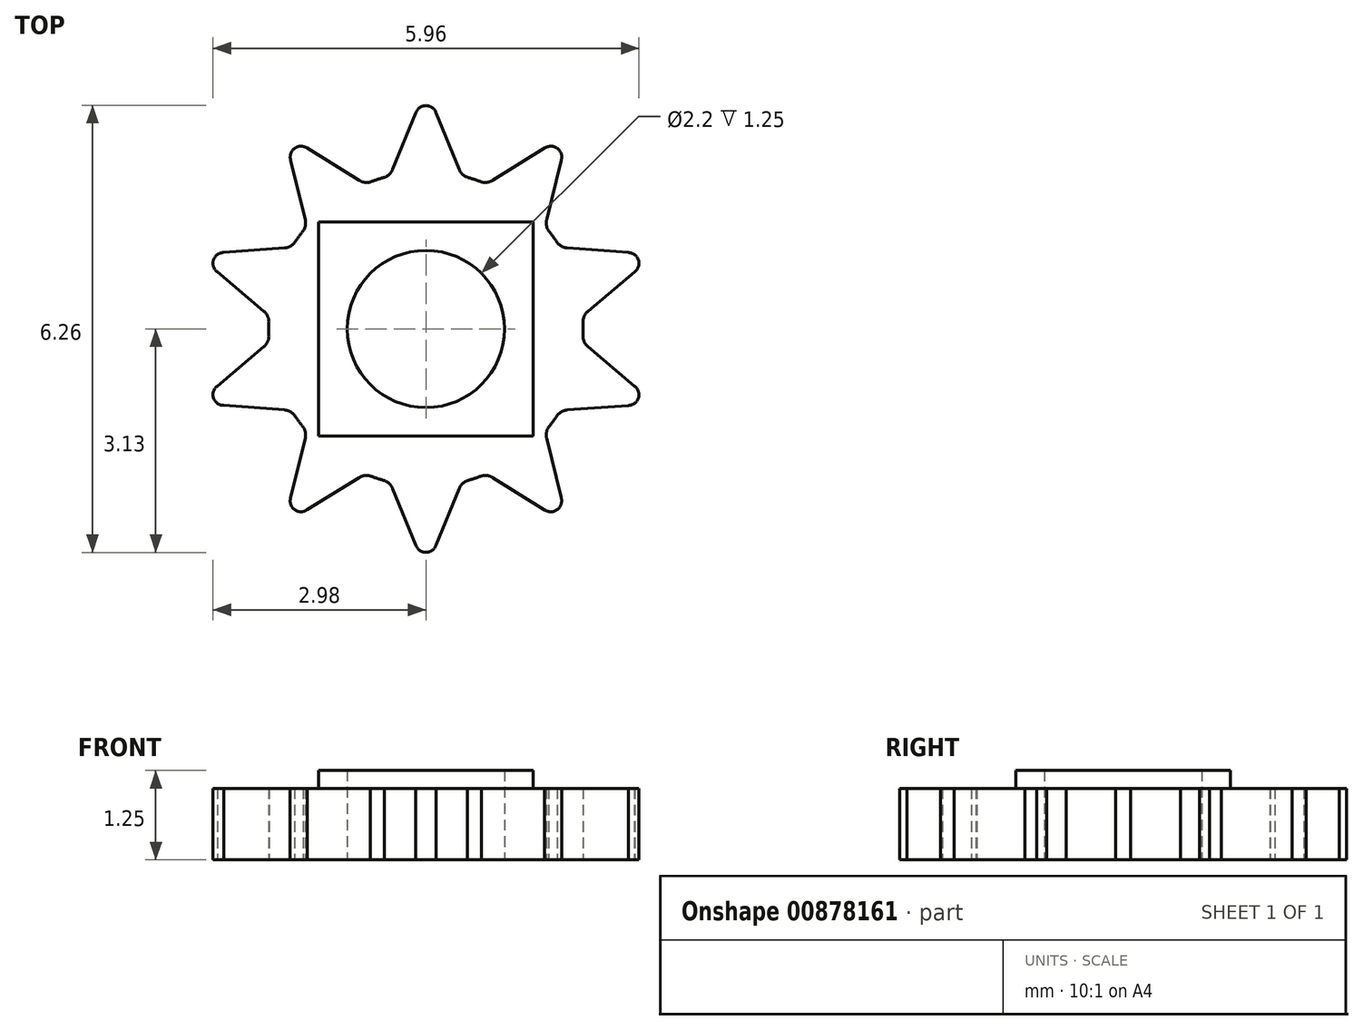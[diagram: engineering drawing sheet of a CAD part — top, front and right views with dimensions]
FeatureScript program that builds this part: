
annotation { "Feature Type Name" : "Feature", "Feature Type Description" : "" }
export const myFeature = defineFeature(function(context is Context, id is Id, definition is map)
    precondition{}
    {
        {
            var Q0;
            Q0=qCreatedBy(makeId("Top.planeOp"),FACE);
            var sketch = newSketch(context, id + "F0", { "sketchPlane" : qUnion([Q0])});
            skArc(sketch, "E0", {"start": v(-0.6, 0.8) * mm, "mid": v(0, -1) * mm, "end": v(0.6, 0.8) * mm});
            skLineSegment(sketch, "E1", {"start": v(0, 0) * mm, "end": v(0, 0.8) * mm});
            skLineSegment(sketch, "E2", {"start": v(0, 0.8) * mm, "end": v(0.6, 0.8) * mm});
            skLineSegment(sketch, "E3", {"start": v(0.6, 0.8) * mm, "end": v(-0.6, 0.8) * mm});
            skLineSegment(sketch, "E4", {"start": v(0, 0) * mm, "end": v(0, 3.13) * mm});
            skArc(sketch, "E5", {"start": v(-0.61, 2.11) * mm, "mid": v(-0.52, 2.15) * mm, "end": v(-0.47, 2.23) * mm});
            skArc(sketch, "E6", {"start": v(0.47, 2.23) * mm, "mid": v(0.52, 2.15) * mm, "end": v(0.61, 2.11) * mm});
            skLineSegment(sketch, "E7", {"start": v(0.47, 2.23) * mm, "end": v(0.14, 3.02) * mm});
            skLineSegment(sketch, "E8", {"start": v(-0.14, 3.02) * mm, "end": v(-0.47, 2.23) * mm});
            skPoint(sketch, "E9.start.orphan", {"position": v(-0.5, 4.18) * mm});
            skPoint(sketch, "E10.orphan", {"position": v(0.5, 4.18) * mm});
            skPoint(sketch, "E11.orphan", {"position": v(-0.5, 3.14) * mm});
            skPoint(sketch, "E12.orphan", {"position": v(0.5, 3.14) * mm});
            skCircle(sketch, "E13", {"center": v(0, 0) * mm, "radius": 2.2 * mm});
            skLineSegment(sketch, "E14", {"start": v(0, 2.2) * mm, "end": v(0, -0.08) * mm});
            skCircle(sketch, "E15", {"center": v(0, 2.98) * mm, "radius": 0.15 * mm});
            skLineSegment(sketch, "E16.trimOffspring", {"start": v(0, 3.18) * mm, "end": v(0, 3.18) * mm});
            skSolve(sketch);
        }
        {
            var Q0;
            Q0=qSketchRegion(id+"F0",true);
            extrude(context, id + "F1", {"entities" : qUnion([Q0]), "depth" : 1 * mm, "offsetDistance" : 25 * mm});
        }
        {
            var Q0;
            Q0=makeQuery(id+"F1.opExtrude","SWEPT_FACE",FACE,{"disambiguationData":[OSD([sQuery(id+"F0.wireOp",EDGE,"E7")])]});
            var Q1;
            Q1=makeQuery(id+"F1.opExtrude","SWEPT_FACE",FACE,{"disambiguationData":[OSD([sQuery(id+"F0.wireOp",EDGE,"E6")])]});
            var Q2;
            Q2=makeQuery(id+"F1.opExtrude","SWEPT_FACE",FACE,{"disambiguationData":[OSD([sQuery(id+"F0.wireOp",EDGE,"E15")])]});
            var Q3;
            Q3=makeQuery(id+"F1.opExtrude","SWEPT_FACE",FACE,{"disambiguationData":[OSD([sQuery(id+"F0.wireOp",EDGE,"E8")])]});
            var Q4;
            Q4=makeQuery(id+"F1.opExtrude","SWEPT_FACE",FACE,{"disambiguationData":[OSD([sQuery(id+"F0.wireOp",EDGE,"E5")])]});
            var Q5;
            Q5=makeQuery(id+"F1.opExtrude","SWEPT_FACE",FACE,{"disambiguationData":[OSD([sQuery(id+"F0.wireOp",EDGE,"E0")])]});
            circularPattern(context, id + "F2", {"patternType" : PatternType.FACE, "faces" : qUnion([Q0, Q1, Q2, Q3, Q4]), "axis" : qUnion([Q5]), "angle" : 360 * degree, "instanceCount" : 10, "equalSpace" : true});
        }
        {
            var Q0;
            Q0=makeQuery(id+"F1.opExtrude","CAP_FACE",FACE,{"disambiguationData":[OSD([sQuery(id+"F0.wireOp",EDGE,"fvcJd2ya-tVhh-xxZW-4oz9-YDaeGeMDFEol"),sQuery(id+"F0.wireOp",EDGE,"E0"),sQuery(id+"F0.wireOp",EDGE,"E3"),sQuery(id+"F0.wireOp",EDGE,"eaARCY1Z-NOzu-Sdc5-bvnF-4fAZ0A6SJQx6"),sQuery(id+"F0.wireOp",EDGE,"E9"),sQuery(id+"F0.wireOp",EDGE,"5273f35b-b4da-4427-86f1-7bf0b3b0f4d40.MirrorCS"),sQuery(id+"F0.wireOp",EDGE,"358262c5-c650-46fa-82b1-be198478d2b90.MirrorCS")])],"isStart":false});
            var sketch = newSketch(context, id + "F3", { "sketchPlane" : qUnion([Q0])});
            skLineSegment(sketch, "E17.bottom", {"start": v(1.5, 1.5) * mm, "end": v(-1.5, 1.5) * mm});
            skLineSegment(sketch, "E17.top", {"start": v(1.5, -1.5) * mm, "end": v(-1.5, -1.5) * mm});
            skLineSegment(sketch, "E17.left", {"start": v(1.5, 1.5) * mm, "end": v(1.5, -1.5) * mm});
            skLineSegment(sketch, "E17.right", {"start": v(-1.5, 1.5) * mm, "end": v(-1.5, -1.5) * mm});
            skPoint(sketch, "E17.middle", {"position": v(0, 0) * mm});
            skSolve(sketch);
        }
        {
            var Q0;
            Q0=qSketchRegion(id+"F3",true);
            extrude(context, id + "F4", {"entities" : qUnion([Q0]), "operationType" : NewBodyOperationType.REMOVE, "oppositeDirection" : true, "depth" : .25 * mm, "offsetDistance" : 25 * mm});
        }
        {
            var Q0;
            Q0=qSketchRegion(id+"F0",true);
            extrude(context, id + "F5", {"entities" : qUnion([Q0]), "operationType" : NewBodyOperationType.ADD, "depth" : 1 * mm, "offsetDistance" : 25 * mm});
        }
        {
            var Q0;
            Q0=makeQuery(id+"F3.imprint","IMPRINT",FACE,{"disambiguationData":[TD([[makeQuery(id+"F3.imprint","IMPRINT",EDGE,{"derivedFrom":sQuery(id+"F3.wireOp",EDGE,"E17.bottom")}),1.0]])]});
            extrude(context, id + "F6", {"entities" : qUnion([Q0]), "operationType" : NewBodyOperationType.ADD, "depth" : .25 * mm, "offsetDistance" : 25 * mm});
        }
        {
            var Q0;
            Q0=makeQuery(id+"F3.imprint","IMPRINT",FACE,{"disambiguationData":[TD([[makeQuery(id+"F3.imprint","IMPRINT",EDGE,{"derivedFrom":makeQuery(id+"F1.opExtrude","CAP_EDGE",EDGE,{"disambiguationData":[OSD([sQuery(id+"F0.wireOp",EDGE,"E0")])],"isStart":false})}),1.0]])]});
            var sketch = newSketch(context, id + "F7", { "sketchPlane" : qUnion([Q0])});
            skCircle(sketch, "E18", {"center": v(0, 0) * mm, "radius": 1.1 * mm});
            skSolve(sketch);
        }
        {
            var Q0;
            Q0 = qSketchRegion(id + "F7", true);
            extrude(context, id + "F8", {"entities" : qUnion([Q0]), "operationType" : NewBodyOperationType.REMOVE, "endBound" : BoundingType.SYMMETRIC, "depth" : 25 * mm, "offsetDistance" : 25 * mm});
        }
    });
